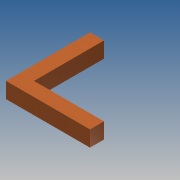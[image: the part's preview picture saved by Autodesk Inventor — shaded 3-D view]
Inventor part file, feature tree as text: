
AUTODESK INVENTOR PART (.ipt)
format: ipt  version: 2013 (Build 170138000, 138)  size: 78,336 bytes
history: native  units: in
note: dims shown in document units (in); Inventor stores cm internally (conversion verified against a paired STEP export)
features: extrude x1, sketch x1
ambient origin geometry x8: Origin, YZ Plane, XZ Plane, XY Plane, X Axis, Y Axis, Z Axis, Center Point
bodies: Solid1 (feature_tree)
feature tree (2):
  extrude  "Extrusion1"  Depth=96.0in
  sketch  "Sketch1"  dims[d0=96.0in d2=96.0in d3=16.0in d4=18.0in d5=0.0in]
